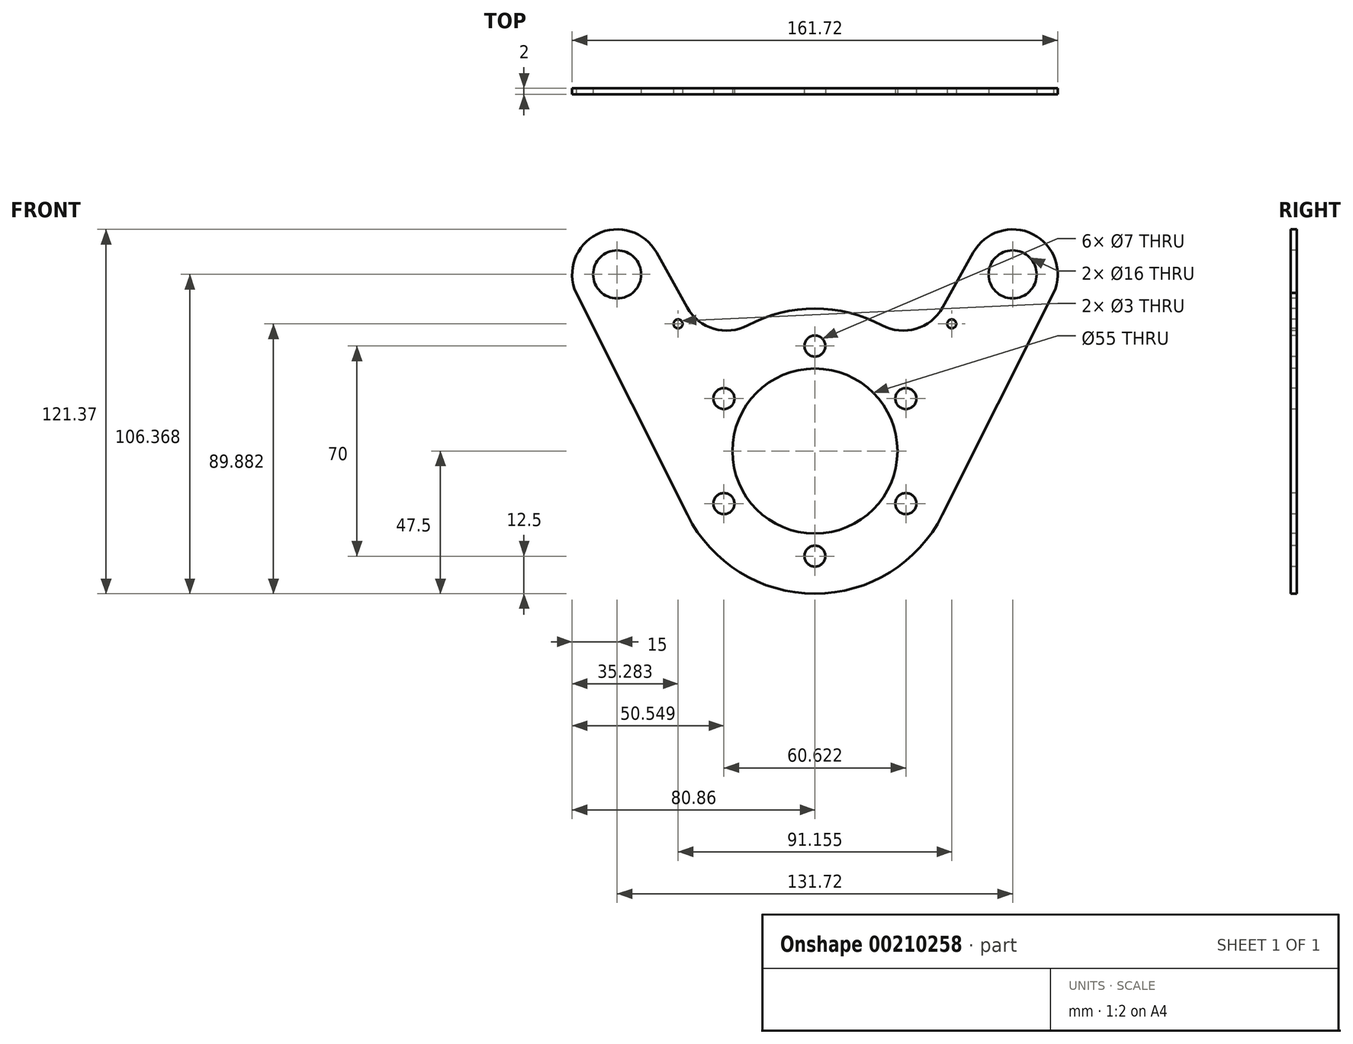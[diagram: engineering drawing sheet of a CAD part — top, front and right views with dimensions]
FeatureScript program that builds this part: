
annotation { "Feature Type Name" : "Feature", "Feature Type Description" : "" }
export const myFeature = defineFeature(function(context is Context, id is Id, definition is map)
    precondition{}
    {
        {
            var Q0;
            Q0=qCreatedBy(makeId("Front.planeOp"),FACE);
            var sketch = newSketch(context, id + "F0", { "sketchPlane" : qUnion([Q0])});
            skCircle(sketch, "E0", {"center": v(0, 0) * mm, "radius": 27.5 * mm});
            skCircle(sketch, "E1", {"center": v(0, 35) * mm, "radius": 3 * mm});
            skCircle(sketch, "E2.1.0", {"center": v(-30.31, 17.5) * mm, "radius": 3 * mm});
            skCircle(sketch, "E2.2.0", {"center": v(-30.31, -17.5) * mm, "radius": 3 * mm});
            skCircle(sketch, "E2.3.0", {"center": v(0, -35) * mm, "radius": 3 * mm});
            skCircle(sketch, "E2.4.0", {"center": v(30.31, -17.5) * mm, "radius": 3 * mm});
            skCircle(sketch, "E2.5.0", {"center": v(30.31, 17.5) * mm, "radius": 3 * mm});
            skLineSegment(sketch, "E3", {"start": v(0, -80) * mm, "end": v(-18, -80) * mm});
            skArc(sketch, "E4", {"start": v(-37.9, -38.47) * mm, "mid": v(-59.22, -23.35) * mm, "end": v(-84, -15) * mm});
            skArc(sketch, "E5", {"start": v(-18, -80) * mm, "mid": v(-25.25, -57.94) * mm, "end": v(-37.9, -38.47) * mm});
            skLineSegment(sketch, "E6", {"start": v(-84, 30) * mm, "end": v(-84, -15) * mm});
            skArc(sketch, "E7", {"start": v(0, 48) * mm, "mid": v(-43.03, 43.8) * mm, "end": v(-84, 30) * mm});
            skArc(sketch, "E8.MirrorCS", {"start": v(0, 48) * mm, "mid": v(43.03, 43.8) * mm, "end": v(84, 30) * mm});
            skLineSegment(sketch, "E9.MirrorCS", {"start": v(84, 30) * mm, "end": v(84, -15) * mm});
            skLineSegment(sketch, "E10.MirrorCS", {"start": v(84, -15) * mm, "end": v(84, -15) * mm});
            skArc(sketch, "E11.MirrorCS", {"start": v(37.9, -38.47) * mm, "mid": v(59.22, -23.35) * mm, "end": v(84, -15) * mm});
            skArc(sketch, "E12.MirrorCS", {"start": v(18, -80) * mm, "mid": v(25.25, -57.94) * mm, "end": v(37.9, -38.47) * mm});
            skLineSegment(sketch, "E13.MirrorCS", {"start": v(0, -80) * mm, "end": v(18, -80) * mm});
            skLineSegment(sketch, "E14", {"start": v(0, 0) * mm, "end": v(37.9, -38.47) * mm});
            skSolve(sketch);
        }
        {
            var Q0;
            Q0=qCreatedBy(makeId("Front.planeOp"),FACE);
            var sketch = newSketch(context, id + "F1", { "sketchPlane" : qUnion([Q0])});
            skLineSegment(sketch, "E15", {"start": v(-50, 57.83) * mm, "end": v(-50, 58) * mm});
            skLineSegment(sketch, "E16", {"start": v(-56.51, 67.37) * mm, "end": v(-56.51, 67.37) * mm});
            skPoint(sketch, "E17.visualSharp", {"position": v(-50, 64.95) * mm});
            skArc(sketch, "E17.filletArc", {"start": v(-50, 58) * mm, "mid": v(-51.79, 63.7) * mm, "end": v(-56.51, 67.37) * mm});
            skPoint(sketch, "E18.visualSharp", {"position": v(-50, 48) * mm});
            skLineSegment(sketch, "E19", {"start": v(0, 0) * mm, "end": v(0, 35) * mm});
            skCircle(sketch, "E20", {"center": v(-65, 52.37) * mm, "radius": 6.25 * mm});
            skPoint(sketch, "E21.center", {"position": v(0, 0) * mm});
            skCircle(sketch, "E22", {"center": v(-65, -42.63) * mm, "radius": 6.25 * mm});
            skLineSegment(sketch, "E23", {"start": v(-80, 57.37) * mm, "end": v(-80, -47.63) * mm});
            skLineSegment(sketch, "E24", {"start": v(-70, -57.63) * mm, "end": v(0, -57.63) * mm});
            skPoint(sketch, "E25.visualSharp", {"position": v(-80, -57.63) * mm});
            skArc(sketch, "E25.filletArc", {"start": v(-80, -47.63) * mm, "mid": v(-77.07, -54.7) * mm, "end": v(-70, -57.63) * mm});
            skLineSegment(sketch, "E26", {"start": v(-70, 67.37) * mm, "end": v(-56.51, 67.37) * mm});
            skPoint(sketch, "E27.visualSharp", {"position": v(-80, 67.37) * mm});
            skArc(sketch, "E27.filletArc", {"start": v(-70, 67.37) * mm, "mid": v(-77.07, 64.44) * mm, "end": v(-80, 57.37) * mm});
            skLineSegment(sketch, "E28", {"start": v(0, 35) * mm, "end": v(0, 48) * mm});
            skLineSegment(sketch, "E29", {"start": v(0, 48) * mm, "end": v(-40, 48) * mm});
            skLineSegment(sketch, "E30", {"start": v(-50, 58) * mm, "end": v(-50, 58) * mm});
            skArc(sketch, "E31.filletArc", {"start": v(-50, 58) * mm, "mid": v(-47.07, 50.93) * mm, "end": v(-40, 48) * mm});
            skCircle(sketch, "E32", {"center": v(-30.31, 17.64) * mm, "radius": 3 * mm});
            skCircle(sketch, "E33", {"center": v(0, 35) * mm, "radius": 3 * mm});
            skCircle(sketch, "E34.MirrorC", {"center": v(0, -35) * mm, "radius": 3 * mm});
            skCircle(sketch, "E35.MirrorC", {"center": v(-30.31, -17.64) * mm, "radius": 3 * mm});
            skCircle(sketch, "E36.MirrorC", {"center": v(30.31, 17.64) * mm, "radius": 3 * mm});
            skCircle(sketch, "E37.MirrorC", {"center": v(30.31, -17.64) * mm, "radius": 3 * mm});
            skLineSegment(sketch, "E38.MirrorCS", {"start": v(70, -57.63) * mm, "end": v(0, -57.63) * mm});
            skArc(sketch, "E39.MirrorCS", {"start": v(80, -47.63) * mm, "mid": v(77.07, -54.7) * mm, "end": v(70, -57.63) * mm});
            skLineSegment(sketch, "E40.MirrorCS", {"start": v(80, 57.37) * mm, "end": v(80, -47.63) * mm});
            skArc(sketch, "E41.MirrorCS", {"start": v(70, 67.37) * mm, "mid": v(77.07, 64.44) * mm, "end": v(80, 57.37) * mm});
            skArc(sketch, "E42.MirrorCS", {"start": v(50, 58) * mm, "mid": v(47.07, 50.93) * mm, "end": v(40, 48) * mm});
            skLineSegment(sketch, "E43.MirrorCS", {"start": v(0, 48) * mm, "end": v(40, 48) * mm});
            skArc(sketch, "E44.MirrorCS", {"start": v(50, 58) * mm, "mid": v(51.79, 63.7) * mm, "end": v(56.51, 67.37) * mm});
            skLineSegment(sketch, "E45.MirrorCS", {"start": v(70, 67.37) * mm, "end": v(56.51, 67.37) * mm});
            skCircle(sketch, "E46.MirrorC", {"center": v(65, 52.37) * mm, "radius": 6.25 * mm});
            skCircle(sketch, "E47.MirrorC", {"center": v(65, -42.63) * mm, "radius": 6.25 * mm});
            skSolve(sketch);
        }
        {
            var Q0;
            Q0=qCreatedBy(makeId("Front.planeOp"),FACE);
            var sketch = newSketch(context, id + "F2", { "sketchPlane" : qUnion([Q0])});
            skCircle(sketch, "E48", {"center": v(0, 0) * mm, "radius": 27.5 * mm});
            skCircle(sketch, "E49", {"center": v(-65.86, 58.87) * mm, "radius": 8 * mm});
            skArc(sketch, "E50", {"start": v(-52.76, 66.17) * mm, "mid": v(-73.17, 71.97) * mm, "end": v(-78.96, 51.56) * mm});
            skArc(sketch, "E51", {"start": v(-42.47, -21.28) * mm, "mid": v(0, -47.5) * mm, "end": v(42.47, -21.28) * mm});
            skLineSegment(sketch, "E52", {"start": v(-79.56, 52.75) * mm, "end": v(-42.47, -21.28) * mm});
            skLineSegment(sketch, "E53", {"start": v(-52.76, 66.17) * mm, "end": v(-42.53, 47.83) * mm});
            skPoint(sketch, "E54.visualSharp", {"position": v(-34.23, 32.94) * mm});
            skArc(sketch, "E54.filletArc", {"start": v(-42.53, 47.83) * mm, "mid": v(-33.66, 40.75) * mm, "end": v(-22.37, 41.9) * mm});
            skArc(sketch, "E55.MirrorCS", {"start": v(42.53, 47.83) * mm, "mid": v(33.66, 40.75) * mm, "end": v(22.37, 41.9) * mm});
            skLineSegment(sketch, "E56.MirrorCS", {"start": v(52.76, 66.17) * mm, "end": v(42.53, 47.83) * mm});
            skArc(sketch, "E57.MirrorCS", {"start": v(52.76, 66.17) * mm, "mid": v(73.17, 71.97) * mm, "end": v(78.96, 51.56) * mm});
            skCircle(sketch, "E58.MirrorC", {"center": v(65.86, 58.87) * mm, "radius": 8 * mm});
            skLineSegment(sketch, "E59.MirrorCS", {"start": v(79.56, 52.75) * mm, "end": v(42.47, -21.28) * mm});
            skArc(sketch, "E60.trimOffspring", {"start": v(22.37, 41.9) * mm, "mid": v(0, 47.5) * mm, "end": v(-22.37, 41.9) * mm});
            skCircle(sketch, "E61", {"center": v(0, 35) * mm, "radius": 3.5 * mm});
            skCircle(sketch, "E62.1.0", {"center": v(-30.31, 17.5) * mm, "radius": 3.5 * mm});
            skCircle(sketch, "E62.2.0", {"center": v(-30.31, -17.5) * mm, "radius": 3.5 * mm});
            skCircle(sketch, "E62.3.0", {"center": v(0, -35) * mm, "radius": 3.5 * mm});
            skCircle(sketch, "E62.4.0", {"center": v(30.31, -17.5) * mm, "radius": 3.5 * mm});
            skCircle(sketch, "E62.5.0", {"center": v(30.31, 17.5) * mm, "radius": 3.5 * mm});
            skCircle(sketch, "E63", {"center": v(-45.58, 42.38) * mm, "radius": 1.5 * mm});
            skCircle(sketch, "E64.MirrorC", {"center": v(45.58, 42.38) * mm, "radius": 1.5 * mm});
            skSolve(sketch);
        }
        {
            var Q0;
            Q0=makeQuery(id+"F2.imprint","IMPRINT",FACE,{"disambiguationData":[TD([[makeQuery(id+"F2.imprint","IMPRINT",EDGE,{"derivedFrom":sQuery(id+"F2.wireOp",EDGE,"E48")}),-1.0]])]});
            extrude(context, id + "F3", {"entities" : qUnion([Q0]), "oppositeDirection" : true, "depth" : 2 * mm, "offsetDistance" : 25 * mm});
        }
    });
